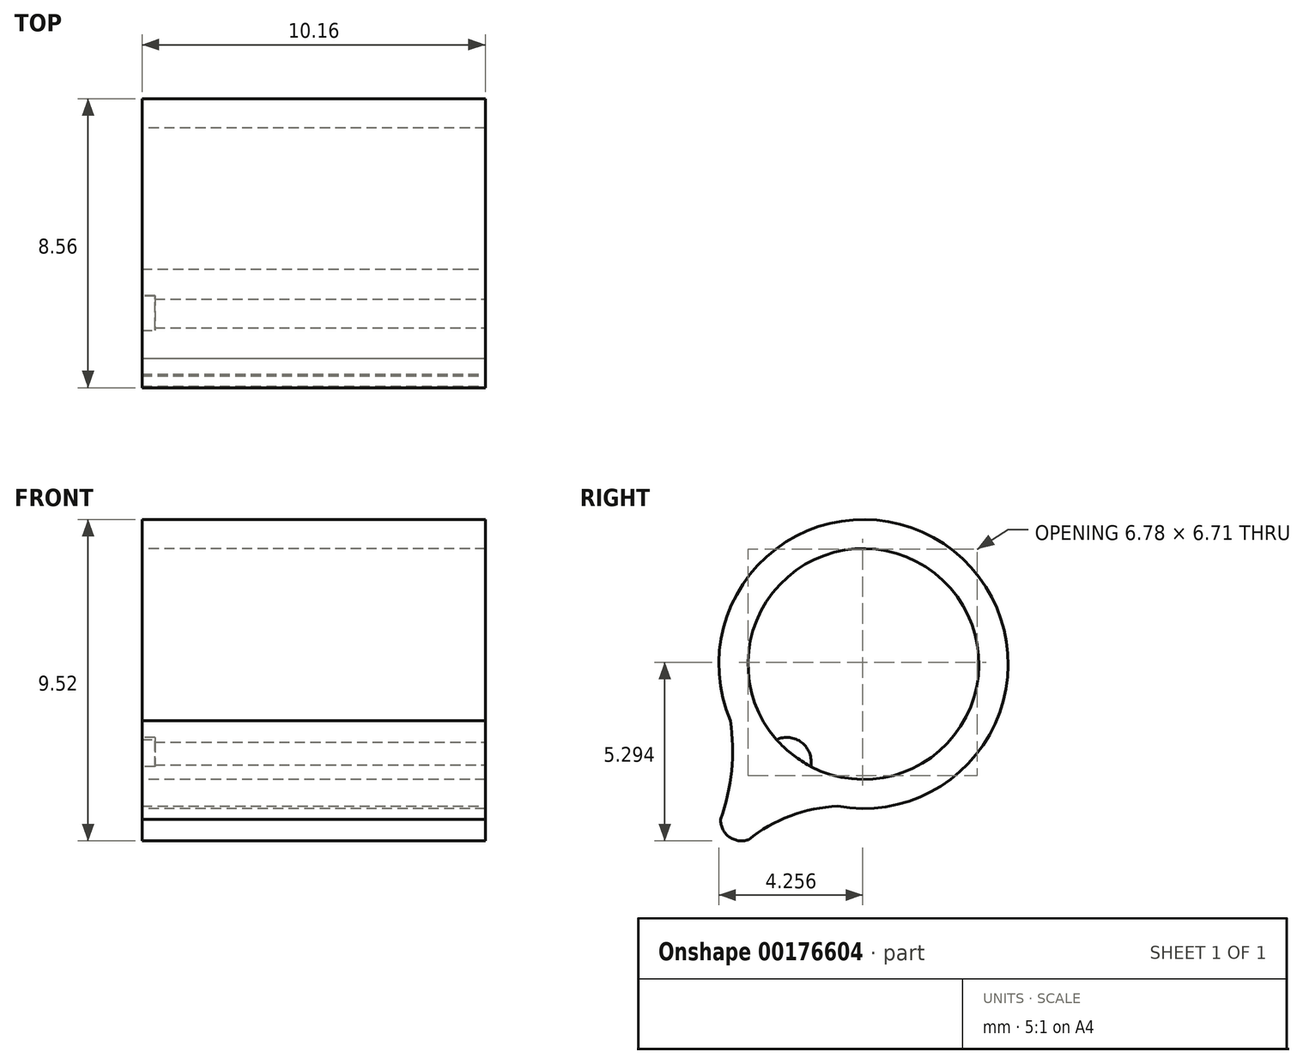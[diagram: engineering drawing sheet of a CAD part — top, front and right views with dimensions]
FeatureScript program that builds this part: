
annotation { "Feature Type Name" : "Feature", "Feature Type Description" : "" }
export const myFeature = defineFeature(function(context is Context, id is Id, definition is map)
    precondition{}
    {
        {
            var Q0;
            Q0=qCreatedBy(makeId("Right.planeOp"),FACE);
            var sketch = newSketch(context, id + "F0", { "sketchPlane" : qUnion([Q0])});
            skCircle(sketch, "E0", {"center": v(0, 0) * mm, "radius": 3.42 * mm});
            skCircle(sketch, "E1", {"center": v(0, 0) * mm, "radius": 4.28 * mm});
            skArc(sketch, "E2", {"start": v(-1.56, -3.04) * mm, "mid": v(-1.82, -2.33) * mm, "end": v(-2.58, -2.24) * mm});
            skSolve(sketch);
        }
        {
            var Q0;
            Q0 = qSketchRegion(id + "F0", true);
            var Q1;
            {var subQ0=sQuery(id+"F0.wireOp",EDGE,"jWD0S3JV-Qj1H-wpq8-sqaW-AQuyGT6iRK6i");Q1=makeQuery(id+"F0.imprint","IMPRINT",FACE,{"disambiguationData":[TD([[makeQuery(id+"F0.imprint","IMPRINT",EDGE,{"derivedFrom":subQ0}),1.0]])]});}
            var Q2;
            {var subQ0=sQuery(id+"F0.wireOp",EDGE,"E2");Q2=makeQuery(id+"F0.imprint","IMPRINT",FACE,{"disambiguationData":[TD([[makeQuery(id+"F0.imprint","IMPRINT",EDGE,{"derivedFrom":subQ0}),1.0]])]});}
            extrude(context, id + "F1", {"entities" : qUnion([Q0, Q1, Q2]), "depth" : 8.9 * mm});
        }
        {
            var Q0;
            Q0=makeQuery(id+"F1.opExtrude","CAP_FACE",FACE,{"disambiguationData":[OSD([sQuery(id+"F0.wireOp",EDGE,"E0"),sQuery(id+"F0.wireOp",EDGE,"E1"),sQuery(id+"F0.wireOp",EDGE,"jWD0S3JV-Qj1H-wpq8-sqaW-AQuyGT6iRK6i"),sQuery(id+"F0.wireOp",EDGE,"E2")])],"isStart":false});
            extrude(context, id + "F2", {"entities" : qUnion([Q0]), "operationType" : NewBodyOperationType.ADD, "depth" : 10.16 * mm});
        }
        {
            var Q0;
            Q0=makeQuery(id+"F1.opExtrude","CAP_FACE",FACE,{"disambiguationData":[OSD([sQuery(id+"F0.wireOp",EDGE,"E0"),sQuery(id+"F0.wireOp",EDGE,"E1"),sQuery(id+"F0.wireOp",EDGE,"jWD0S3JV-Qj1H-wpq8-sqaW-AQuyGT6iRK6i"),sQuery(id+"F0.wireOp",EDGE,"E2")])],"isStart":true});
            extrude(context, id + "F3", {"entities" : qUnion([Q0]), "operationType" : NewBodyOperationType.REMOVE, "oppositeDirection" : true, "depth" : 8.9 * mm});
        }
        {
            var Q0;
            Q0=makeQuery(id+"F2.opExtrude","CAP_FACE",FACE,{"disambiguationData":[OSD([sQuery(id+"F0.wireOp",EDGE,"E0"),sQuery(id+"F0.wireOp",EDGE,"E1"),sQuery(id+"F0.wireOp",EDGE,"jWD0S3JV-Qj1H-wpq8-sqaW-AQuyGT6iRK6i"),sQuery(id+"F0.wireOp",EDGE,"E2")])],"isStart":false});
            var sketch = newSketch(context, id + "F4", { "sketchPlane" : qUnion([Q0])});
            skArc(sketch, "E3", {"start": v(-2.86, -1.87) * mm, "mid": v(-2.1, -2.68) * mm, "end": v(-1.14, -3.22) * mm});
            skArc(sketch, "E4", {"start": v(2.91, 1.78) * mm, "mid": v(2.18, 2.62) * mm, "end": v(1.22, 3.2) * mm});
            skArc(sketch, "E5", {"start": v(-2.58, -2.24) * mm, "mid": v(-2.1, -2.68) * mm, "end": v(-1.56, -3.04) * mm});
            skSolve(sketch);
        }
        {
            var Q0;
            Q0=makeQuery(id+"F4.imprint","IMPRINT",FACE,{"disambiguationData":[TD([[makeQuery(id+"F4.imprint","IMPRINT",EDGE,{"derivedFrom":sQuery(id+"F4.wireOp",EDGE,"E3")}),1.0]])]});
            extrude(context, id + "F5", {"entities" : qUnion([Q0]), "operationType" : NewBodyOperationType.REMOVE, "oppositeDirection" : true, "depth" : 9.78 * mm});
        }
        {
            var Q0;
            Q0=makeQuery(id+"F2.opExtrude","CAP_FACE",FACE,{"disambiguationData":[OSD([sQuery(id+"F0.wireOp",EDGE,"E0"),sQuery(id+"F0.wireOp",EDGE,"E1"),sQuery(id+"F0.wireOp",EDGE,"E2")])],"isStart":false});
            var sketch = newSketch(context, id + "F6", { "sketchPlane" : qUnion([Q0])});
            skLineSegment(sketch, "E6", {"start": v(-2.64, -3.37) * mm, "end": v(0.06, 0.07) * mm});
            skLineSegment(sketch, "E7", {"start": v(0.06, 0.07) * mm, "end": v(-0.76, -4.21) * mm});
            skLineSegment(sketch, "E8", {"start": v(-2.64, -3.37) * mm, "end": v(-3.8, -4.9) * mm});
            skLineSegment(sketch, "E9", {"start": v(-3.8, -4.9) * mm, "end": v(-3.4, -5.2) * mm});
            skLineSegment(sketch, "E10", {"start": v(-3.4, -5.2) * mm, "end": v(-2.23, -3.65) * mm});
            skLineSegment(sketch, "E11", {"start": v(-2.23, -3.65) * mm, "end": v(-3.03, -3.02) * mm});
            skLineSegment(sketch, "E12", {"start": v(-3.03, -3.02) * mm, "end": v(-4.23, -4.6) * mm});
            skLineSegment(sketch, "E13", {"start": v(-4.23, -4.6) * mm, "end": v(-3.8, -4.9) * mm});
            skArc(sketch, "E14", {"start": v(-0.76, -4.21) * mm, "mid": v(-2.17, -4.5) * mm, "end": v(-3.4, -5.2) * mm});
            skArc(sketch, "E15", {"start": v(-4.23, -4.6) * mm, "mid": v(-3.98, -5.11) * mm, "end": v(-3.4, -5.2) * mm});
            skLineSegment(sketch, "E16", {"start": v(0.06, 0.07) * mm, "end": v(-3.93, -1.68) * mm});
            skArc(sketch, "E17", {"start": v(-4.23, -4.6) * mm, "mid": v(-3.9, -3.16) * mm, "end": v(-3.93, -1.68) * mm});
            skSolve(sketch);
        }
        {
            var Q0;
            Q0=makeQuery(id+"F6.imprint","IMPRINT",FACE,{"disambiguationData":[TD([[makeQuery(id+"F6.imprint","IMPRINT",EDGE,{"derivedFrom":sQuery(id+"F6.wireOp",EDGE,"E9")}),-1.0]])]});
            var Q1;
            {var subQ0=sQuery(id+"F6.wireOp",EDGE,"E10");Q1=makeQuery(id+"F6.imprint","IMPRINT",FACE,{"disambiguationData":[TD([[makeQuery(id+"F6.imprint","IMPRINT",EDGE,{"derivedFrom":subQ0}),-1.0]])]});}
            var Q2;
            {var subQ0=sQuery(id+"F6.wireOp",EDGE,"E12");Q2=makeQuery(id+"F6.imprint","IMPRINT",FACE,{"disambiguationData":[TD([[makeQuery(id+"F6.imprint","IMPRINT",EDGE,{"derivedFrom":subQ0}),-1.0]])]});}
            var Q3;
            {var subQ0=sQuery(id+"F6.wireOp",EDGE,"E6");var subQ3=sQuery(id+"F6.wireOp",EDGE,"E11");var subQ4=makeQuery(id+"F6.imprint","INTERSECT",VERTEX,{"derivedFrom":[subQ0,subQ3]});Q3=makeQuery(id+"F6.imprint","IMPRINT",FACE,{"disambiguationData":[TD([[makeQuery(id+"F6.imprint","IMPRINT",EDGE,{"disambiguationData":[TD([[subQ4,1.0]])],"derivedFrom":subQ0}),-1.0]])]});}
            var Q4;
            {var subQ0=sQuery(id+"F6.wireOp",EDGE,"E6");var subQ3=sQuery(id+"F6.wireOp",EDGE,"E11");var subQ4=makeQuery(id+"F6.imprint","INTERSECT",VERTEX,{"derivedFrom":[subQ0,subQ3]});Q4=makeQuery(id+"F6.imprint","IMPRINT",FACE,{"disambiguationData":[TD([[makeQuery(id+"F6.imprint","IMPRINT",EDGE,{"disambiguationData":[TD([[subQ4,1.0]])],"derivedFrom":subQ0}),1.0]])]});}
            var Q5;
            {var subQ0=sQuery(id+"F6.wireOp",EDGE,"E8");Q5=makeQuery(id+"F6.imprint","IMPRINT",FACE,{"disambiguationData":[TD([[makeQuery(id+"F6.imprint","IMPRINT",EDGE,{"derivedFrom":subQ0}),1.0]])]});}
            var Q6;
            {var subQ0=sQuery(id+"F6.wireOp",EDGE,"E8");Q6=makeQuery(id+"F6.imprint","IMPRINT",FACE,{"disambiguationData":[TD([[makeQuery(id+"F6.imprint","IMPRINT",EDGE,{"derivedFrom":subQ0}),-1.0]])]});}
            extrude(context, id + "F7", {"entities" : qUnion([Q0, Q1, Q2, Q3, Q4, Q5, Q6]), "operationType" : NewBodyOperationType.ADD, "oppositeDirection" : true, "depth" : 10.16 * mm});
        }
    });
